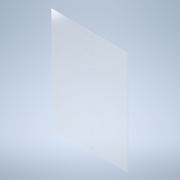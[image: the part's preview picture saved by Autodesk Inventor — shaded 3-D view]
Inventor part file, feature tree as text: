
AUTODESK INVENTOR PART (.ipt)
format: ipt  version: 2020 (Build 240168000, 168)  size: 149,504 bytes
history: native  units: mm
features: sketch x3, hole x3, extrude x1
ambient origin geometry x8: Origin, YZ Plane, XZ Plane, XY Plane, X Axis, Y Axis, Z Axis, Center Point
bodies: Solid1 (feature_tree)
feature tree (7):
  sketch  "Sketch1"  dims[d0=304.8mm d1=419.1mm]
  extrude  "Extrusion1"  Depth=419.1mm
  hole  "Hole1"  [1 undecoded]
  hole  "Hole2"  [1 undecoded]
  hole  "Hole3"  [1 undecoded]
  sketch  "Sketch2"  dims[d2=111.5mm d3=37.5mm]
  sketch  "Sketch3"  dims[d4=37.5mm d6=5.588mm d7=0.0mm d8=7.14375mm d9=6.0mm d10=4.0mm d11=2.0mm d12=90.0deg d13=8.0mm d14=20.594885mm d15=50.0mm d16=50.0mm d17=135.0mm d18=7.14375mm d19=6.0mm d20=4.0mm d21=2.0mm d22=90.0deg d23=8.0mm d24=20.594885mm d25=210.0mm d26=25.4mm d27=57.15mm d28=25.4mm d29=57.15mm d30=47.625mm d31=74.6125mm d33=330.2mm d34=8.73125mm d35=19.05mm d36=9.525mm d37=6.35mm d38=14.3117mm d39=25.4mm d40=90.0deg]
note: 3 required parameter values undecoded (feature->parameter linkage not recoverable at this tier; creation-order binding heuristic only, values carry confidence <= 0.55)
